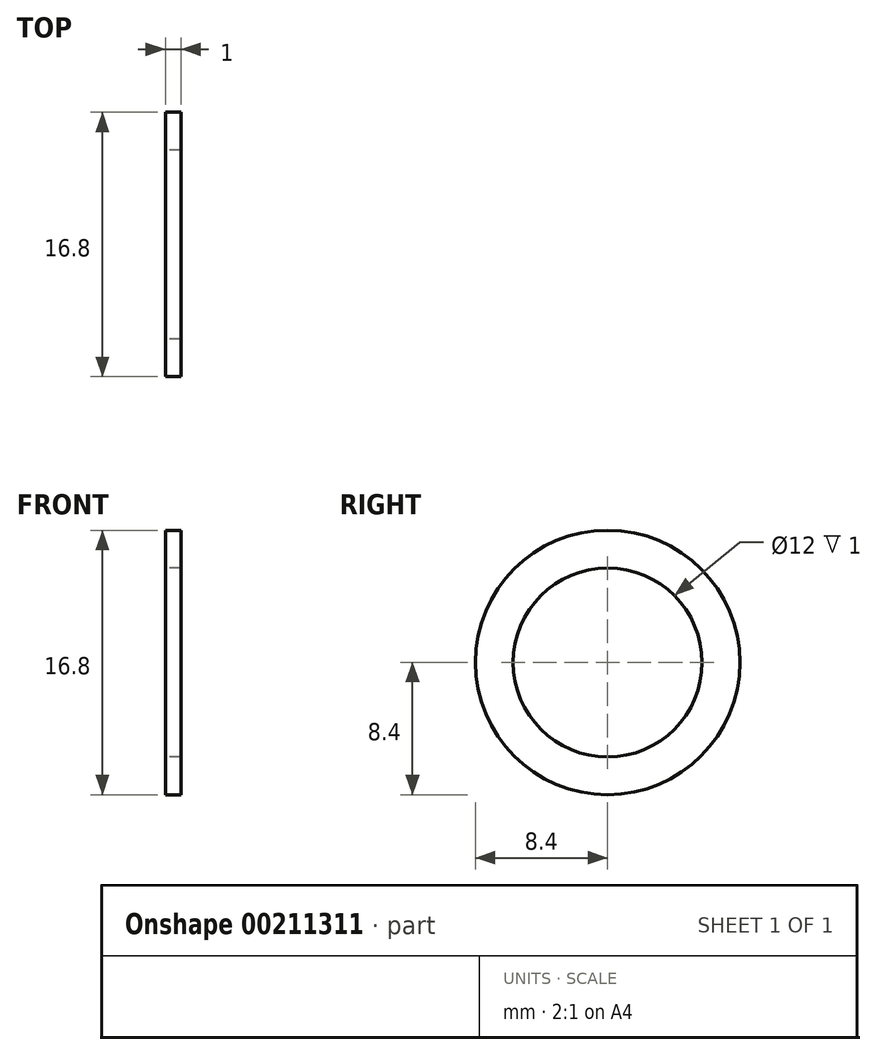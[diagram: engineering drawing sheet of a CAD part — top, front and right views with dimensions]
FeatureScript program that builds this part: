
annotation { "Feature Type Name" : "Feature", "Feature Type Description" : "" }
export const myFeature = defineFeature(function(context is Context, id is Id, definition is map)
    precondition{}
    {
        {
            var Q0;
            Q0=qCreatedBy(makeId("Right.planeOp"),FACE);
            var sketch = newSketch(context, id + "F0", { "sketchPlane" : qUnion([Q0])});
            skCircle(sketch, "E0", {"center": v(0, 0) * mm, "radius": 6 * mm});
            skCircle(sketch, "E1", {"center": v(0, 0) * mm, "radius": 8.4 * mm});
            skSolve(sketch);
        }
        {
            var Q0;
            Q0=qSketchRegion(id+"F0",true);
            extrude(context, id + "F1", {"entities" : qUnion([Q0]), "depth" : 1 * mm});
        }
    });
